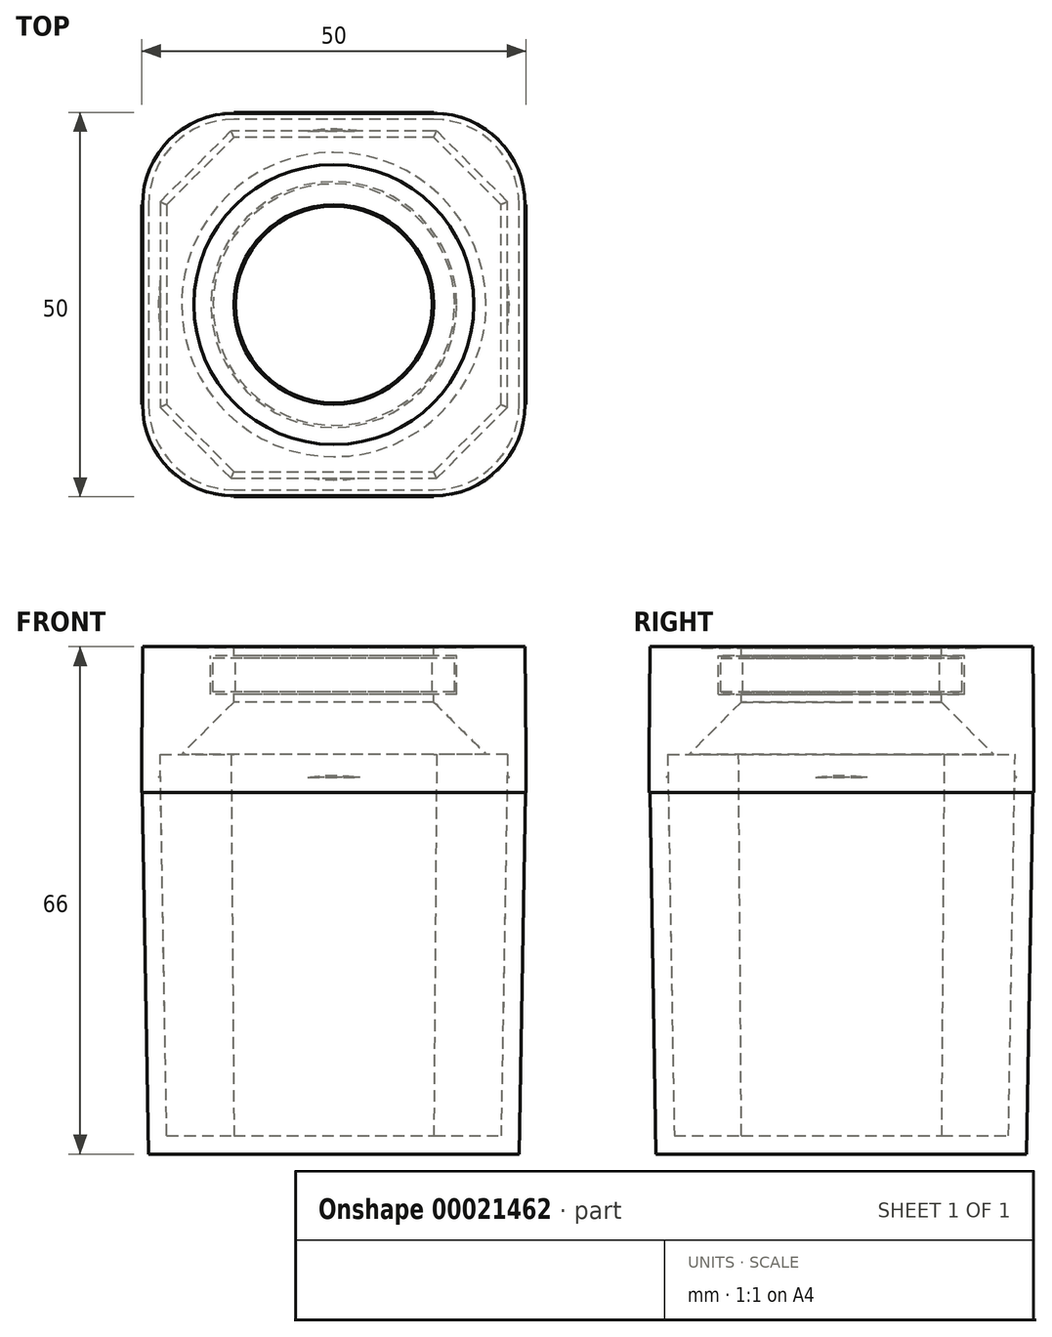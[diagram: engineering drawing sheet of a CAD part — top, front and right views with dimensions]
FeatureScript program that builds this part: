
annotation { "Feature Type Name" : "Feature", "Feature Type Description" : "" }
export const myFeature = defineFeature(function(context is Context, id is Id, definition is map)
    precondition{}
    {
        {
            var Q0;
            Q0=qCreatedBy(makeId("Top.planeOp"),FACE);
            var sketch = newSketch(context, id + "F0", { "sketchPlane" : qUnion([Q0])});
            skLineSegment(sketch, "E0.rect.bottom", {"start": v(13, 25) * mm, "end": v(-13, 25) * mm});
            skLineSegment(sketch, "E0.rect.top", {"start": v(13, -25) * mm, "end": v(-13, -25) * mm});
            skLineSegment(sketch, "E0.rect.left", {"start": v(25, 13) * mm, "end": v(25, -13) * mm});
            skLineSegment(sketch, "E0.rect.right", {"start": v(-25, 13) * mm, "end": v(-25, -13) * mm});
            skPoint(sketch, "E0.rect.middle", {"position": v(0, 0) * mm});
            skPoint(sketch, "E1.visualSharp", {"position": v(-25, 25) * mm});
            skArc(sketch, "E1.filletArc", {"start": v(-13, 25) * mm, "mid": v(-21.49, 21.49) * mm, "end": v(-25, 13) * mm});
            skPoint(sketch, "E2.visualSharp", {"position": v(25, 25) * mm});
            skArc(sketch, "E2.filletArc", {"start": v(25, 13) * mm, "mid": v(21.49, 21.49) * mm, "end": v(13, 25) * mm});
            skPoint(sketch, "E3.visualSharp", {"position": v(25, -25) * mm});
            skArc(sketch, "E3.filletArc", {"start": v(13, -25) * mm, "mid": v(21.49, -21.49) * mm, "end": v(25, -13) * mm});
            skPoint(sketch, "E4.visualSharp", {"position": v(-25, -25) * mm});
            skArc(sketch, "E4.filletArc", {"start": v(-25, -13) * mm, "mid": v(-21.49, -21.49) * mm, "end": v(-13, -25) * mm});
            skSolve(sketch);
        }
        {
            var Q0;
            Q0 = qSketchRegion(id + "F0", true);
            extrude(context, id + "F1", {"entities" : qUnion([Q0]), "oppositeDirection" : true, "depth" : 52 * mm, "hasDraft" : true, "draftAngle" : 1 * degree, "draftPullDirection" : true});
        }
        {
            var Q0;
            Q0=makeQuery(id+"F1.opExtrude","CAP_FACE",FACE,{"disambiguationData":[OSD([sQuery(id+"F0.wireOp",EDGE,"E0.rect.bottom"),sQuery(id+"F0.wireOp",EDGE,"E0.rect.top"),sQuery(id+"F0.wireOp",EDGE,"E0.rect.left"),sQuery(id+"F0.wireOp",EDGE,"E0.rect.right"),sQuery(id+"F0.wireOp",EDGE,"E1.filletArc"),sQuery(id+"F0.wireOp",EDGE,"E2.filletArc"),sQuery(id+"F0.wireOp",EDGE,"E3.filletArc"),sQuery(id+"F0.wireOp",EDGE,"E4.filletArc")])],"isStart":true});
            shell(context, id + "F2", {"entities" : qUnion([Q0]), "thickness" : 2.4 * mm});
        }
        {
            var Q0;
            Q0=makeQuery(id+"F2.opShell","OFFSET_FACE",FACE,{"disambiguationData":[OSD([sQuery(id+"F0.wireOp",EDGE,"E0.rect.bottom"),sQuery(id+"F0.wireOp",EDGE,"E0.rect.top"),sQuery(id+"F0.wireOp",EDGE,"E0.rect.left"),sQuery(id+"F0.wireOp",EDGE,"E0.rect.right"),sQuery(id+"F0.wireOp",EDGE,"E1.filletArc"),sQuery(id+"F0.wireOp",EDGE,"E2.filletArc"),sQuery(id+"F0.wireOp",EDGE,"E3.filletArc"),sQuery(id+"F0.wireOp",EDGE,"E4.filletArc")])]});
            var sketch = newSketch(context, id + "F3", { "sketchPlane" : qUnion([Q0])});
            skLineSegment(sketch, "E5", {"start": v(-13, 21.73) * mm, "end": v(-21.73, 13) * mm});
            skLineSegment(sketch, "E6", {"start": v(13, 21.73) * mm, "end": v(21.73, 13) * mm});
            skLineSegment(sketch, "E7", {"start": v(21.73, -13) * mm, "end": v(13, -21.73) * mm});
            skLineSegment(sketch, "E8", {"start": v(-13, -21.73) * mm, "end": v(-21.73, -13) * mm});
            skSolve(sketch);
        }
        {
            var Q0;
            Q0=sQuery(id+"F3.wireOp",EDGE,"E6");
            cPlane(context, id + "F4", {"entities" : qUnion([Q0]), "cplaneType" : CPlaneType.LINE_ANGLE, "offset" : 150 * mm, "angle" : 179 * degree, "width" : 150 * mm, "height" : 150 * mm});
        }
        {
            var Q0;
            Q0=sQuery(id+"F3.wireOp",EDGE,"E5");
            cPlane(context, id + "F5", {"entities" : qUnion([Q0]), "cplaneType" : CPlaneType.LINE_ANGLE, "offset" : 150 * mm, "angle" : 1 * degree, "width" : 150 * mm, "height" : 150 * mm});
        }
        {
            var Q0;
            Q0=sQuery(id+"F3.wireOp",EDGE,"E8");
            cPlane(context, id + "F6", {"entities" : qUnion([Q0]), "cplaneType" : CPlaneType.LINE_ANGLE, "offset" : 150 * mm, "angle" : 179 * degree, "width" : 150 * mm, "height" : 150 * mm});
        }
        {
            var Q0;
            Q0=sQuery(id+"F3.wireOp",EDGE,"E7");
            cPlane(context, id + "F7", {"entities" : qUnion([Q0]), "cplaneType" : CPlaneType.LINE_ANGLE, "offset" : 150 * mm, "angle" : 179 * degree, "width" : 150 * mm, "height" : 150 * mm});
        }
        {
            var Q0;
            Q0=qCreatedBy(id+"F4.planeOp",FACE);
            var sketch = newSketch(context, id + "F8", { "sketchPlane" : qUnion([Q0])});
            skLineSegment(sketch, "E9.0", {"start": v(13.6, 22.34) * mm, "end": v(22.34, 13.61) * mm});
            skLineSegment(sketch, "E10", {"start": v(13.6, 22.34) * mm, "end": v(12.9, 23.05) * mm});
            skLineSegment(sketch, "E11", {"start": v(22.34, 13.61) * mm, "end": v(23.05, 12.9) * mm});
            skArc(sketch, "E12", {"start": v(23.05, 12.9) * mm, "mid": v(20.3, 20.3) * mm, "end": v(12.9, 23.05) * mm});
            skSolve(sketch);
        }
        {
            var Q0;
            Q0=makeQuery(id+"F8.imprint","IMPRINT",FACE,{"disambiguationData":[TD([[makeQuery(id+"F8.imprint","IMPRINT",EDGE,{"derivedFrom":sQuery(id+"F8.wireOp",EDGE,"E9.0")}),1.0]])]});
            var Q1;
            Q1=makeQuery(id+"F1.opExtrude","CAP_FACE",FACE,{"disambiguationData":[OSD([sQuery(id+"F0.wireOp",EDGE,"E0.rect.bottom"),sQuery(id+"F0.wireOp",EDGE,"E0.rect.top"),sQuery(id+"F0.wireOp",EDGE,"E0.rect.left"),sQuery(id+"F0.wireOp",EDGE,"E0.rect.right"),sQuery(id+"F0.wireOp",EDGE,"E1.filletArc"),sQuery(id+"F0.wireOp",EDGE,"E2.filletArc"),sQuery(id+"F0.wireOp",EDGE,"E3.filletArc"),sQuery(id+"F0.wireOp",EDGE,"E4.filletArc")])],"isStart":true});
            extrude(context, id + "F9", {"entities" : qUnion([Q0]), "operationType" : NewBodyOperationType.ADD, "endBound" : BoundingType.UP_TO_SURFACE, "endBoundEntityFace" : qUnion([Q1]), "depth" : 25 * mm});
        }
        {
            var Q0;
            Q0=qCreatedBy(id+"F5.planeOp",FACE);
            var sketch = newSketch(context, id + "F10", { "sketchPlane" : qUnion([Q0])});
            skLineSegment(sketch, "E13.0", {"start": v(-13.6, -22.34) * mm, "end": v(-22.34, -13.61) * mm});
            skLineSegment(sketch, "E14", {"start": v(-22.34, -13.61) * mm, "end": v(-23.05, -12.9) * mm});
            skLineSegment(sketch, "E15", {"start": v(-13.6, -22.34) * mm, "end": v(-12.9, -23.05) * mm});
            skArc(sketch, "E16", {"start": v(-23.05, -12.9) * mm, "mid": v(-20.3, -20.3) * mm, "end": v(-12.9, -23.05) * mm});
            skSolve(sketch);
        }
        {
            var Q0;
            Q0=makeQuery(id+"F10.imprint","IMPRINT",FACE,{"disambiguationData":[TD([[makeQuery(id+"F10.imprint","IMPRINT",EDGE,{"derivedFrom":sQuery(id+"F10.wireOp",EDGE,"E13.0")}),1.0]])]});
            var Q1;
            {var subQ0=sQuery(id+"F0.wireOp",EDGE,"E4.filletArc");var subQ1=sQuery(id+"F0.wireOp",EDGE,"E3.filletArc");var subQ2=sQuery(id+"F0.wireOp",EDGE,"E2.filletArc");var subQ3=sQuery(id+"F0.wireOp",EDGE,"E1.filletArc");var subQ4=sQuery(id+"F0.wireOp",EDGE,"E0.rect.right");var subQ5=sQuery(id+"F0.wireOp",EDGE,"E0.rect.left");var subQ6=sQuery(id+"F0.wireOp",EDGE,"E0.rect.top");var subQ7=sQuery(id+"F0.wireOp",EDGE,"E0.rect.bottom");Q1=makeQuery(id+"F9.boolean.opBoolean","MERGE",FACE,{"derivedFrom":[makeQuery(id+"F1.opExtrude","CAP_FACE",FACE,{"disambiguationData":[OSD([subQ7,subQ6,subQ5,subQ4,subQ3,subQ2,subQ1,subQ0])],"isStart":true}),makeQuery(id+"F9.opExtrude","CAP_FACE",FACE,{"disambiguationData":[OSD([subQ7,subQ6,subQ5,subQ4,subQ3,subQ2,subQ1,subQ0])],"isStart":false})]});}
            extrude(context, id + "F11", {"entities" : qUnion([Q0]), "operationType" : NewBodyOperationType.ADD, "endBound" : BoundingType.UP_TO_SURFACE, "oppositeDirection" : true, "endBoundEntityFace" : qUnion([Q1]), "depth" : 25 * mm});
        }
        {
            var Q0;
            Q0=qCreatedBy(id+"F6.planeOp",FACE);
            var sketch = newSketch(context, id + "F12", { "sketchPlane" : qUnion([Q0])});
            skLineSegment(sketch, "E17.0", {"start": v(-13.6, 22.34) * mm, "end": v(-22.34, 13.61) * mm});
            skLineSegment(sketch, "E18", {"start": v(-22.34, 13.61) * mm, "end": v(-23.05, 12.9) * mm});
            skLineSegment(sketch, "E19", {"start": v(-13.6, 22.34) * mm, "end": v(-12.9, 23.05) * mm});
            skArc(sketch, "E20", {"start": v(-12.9, 23.05) * mm, "mid": v(-20.3, 20.3) * mm, "end": v(-23.05, 12.9) * mm});
            skSolve(sketch);
        }
        {
            var Q0;
            Q0=makeQuery(id+"F12.imprint","IMPRINT",FACE,{"disambiguationData":[TD([[makeQuery(id+"F12.imprint","IMPRINT",EDGE,{"derivedFrom":sQuery(id+"F12.wireOp",EDGE,"E17.0")}),-1.0]])]});
            var Q1;
            {var subQ0=sQuery(id+"F0.wireOp",EDGE,"E4.filletArc");var subQ1=sQuery(id+"F0.wireOp",EDGE,"E3.filletArc");var subQ2=sQuery(id+"F0.wireOp",EDGE,"E2.filletArc");var subQ3=sQuery(id+"F0.wireOp",EDGE,"E1.filletArc");var subQ4=sQuery(id+"F0.wireOp",EDGE,"E0.rect.right");var subQ5=sQuery(id+"F0.wireOp",EDGE,"E0.rect.left");var subQ6=sQuery(id+"F0.wireOp",EDGE,"E0.rect.top");var subQ7=sQuery(id+"F0.wireOp",EDGE,"E0.rect.bottom");Q1=makeQuery(id+"F11.boolean.opBoolean","MERGE",FACE,{"derivedFrom":[makeQuery(id+"F9.boolean.opBoolean","MERGE",FACE,{"derivedFrom":[makeQuery(id+"F1.opExtrude","CAP_FACE",FACE,{"disambiguationData":[OSD([subQ7,subQ6,subQ5,subQ4,subQ3,subQ2,subQ1,subQ0])],"isStart":true}),makeQuery(id+"F9.opExtrude","CAP_FACE",FACE,{"disambiguationData":[OSD([subQ7,subQ6,subQ5,subQ4,subQ3,subQ2,subQ1,subQ0])],"isStart":false})]}),makeQuery(id+"F11.opExtrude","CAP_FACE",FACE,{"disambiguationData":[OSD([subQ7,subQ6,subQ5,subQ4,subQ3,subQ2,subQ1,subQ0])],"isStart":false})]});}
            extrude(context, id + "F13", {"entities" : qUnion([Q0]), "operationType" : NewBodyOperationType.ADD, "endBound" : BoundingType.UP_TO_SURFACE, "oppositeDirection" : true, "endBoundEntityFace" : qUnion([Q1]), "depth" : 25 * mm});
        }
        {
            var Q0;
            Q0=qCreatedBy(id+"F7.planeOp",FACE);
            var sketch = newSketch(context, id + "F14", { "sketchPlane" : qUnion([Q0])});
            skLineSegment(sketch, "E21.0", {"start": v(22.34, -13.61) * mm, "end": v(13.6, -22.34) * mm});
            skLineSegment(sketch, "E22", {"start": v(13.6, -22.34) * mm, "end": v(12.9, -23.05) * mm});
            skLineSegment(sketch, "E23", {"start": v(22.34, -13.61) * mm, "end": v(23.05, -12.9) * mm});
            skArc(sketch, "E24", {"start": v(12.9, -23.05) * mm, "mid": v(20.3, -20.3) * mm, "end": v(23.05, -12.9) * mm});
            skSolve(sketch);
        }
        {
            var Q0;
            Q0=makeQuery(id+"F14.imprint","IMPRINT",FACE,{"disambiguationData":[TD([[makeQuery(id+"F14.imprint","IMPRINT",EDGE,{"derivedFrom":sQuery(id+"F14.wireOp",EDGE,"E21.0")}),1.0]])]});
            var Q1;
            {var subQ0=sQuery(id+"F0.wireOp",EDGE,"E4.filletArc");var subQ1=sQuery(id+"F0.wireOp",EDGE,"E3.filletArc");var subQ2=sQuery(id+"F0.wireOp",EDGE,"E2.filletArc");var subQ3=sQuery(id+"F0.wireOp",EDGE,"E1.filletArc");var subQ4=sQuery(id+"F0.wireOp",EDGE,"E0.rect.right");var subQ5=sQuery(id+"F0.wireOp",EDGE,"E0.rect.left");var subQ6=sQuery(id+"F0.wireOp",EDGE,"E0.rect.top");var subQ7=sQuery(id+"F0.wireOp",EDGE,"E0.rect.bottom");Q1=makeQuery(id+"F13.boolean.opBoolean","MERGE",FACE,{"derivedFrom":[makeQuery(id+"F11.boolean.opBoolean","MERGE",FACE,{"derivedFrom":[makeQuery(id+"F9.boolean.opBoolean","MERGE",FACE,{"derivedFrom":[makeQuery(id+"F1.opExtrude","CAP_FACE",FACE,{"disambiguationData":[OSD([subQ7,subQ6,subQ5,subQ4,subQ3,subQ2,subQ1,subQ0])],"isStart":true}),makeQuery(id+"F9.opExtrude","CAP_FACE",FACE,{"disambiguationData":[OSD([subQ7,subQ6,subQ5,subQ4,subQ3,subQ2,subQ1,subQ0])],"isStart":false})]}),makeQuery(id+"F11.opExtrude","CAP_FACE",FACE,{"disambiguationData":[OSD([subQ7,subQ6,subQ5,subQ4,subQ3,subQ2,subQ1,subQ0])],"isStart":false})]}),makeQuery(id+"F13.opExtrude","CAP_FACE",FACE,{"disambiguationData":[OSD([subQ7,subQ6,subQ5,subQ4,subQ3,subQ2,subQ1,subQ0])],"isStart":false})]});}
            extrude(context, id + "F15", {"entities" : qUnion([Q0]), "operationType" : NewBodyOperationType.ADD, "endBound" : BoundingType.UP_TO_SURFACE, "endBoundEntityFace" : qUnion([Q1]), "depth" : 25 * mm});
        }
        {
            var Q0;
            Q0=qCreatedBy(makeId("Top.planeOp"),FACE);
            var sketch = newSketch(context, id + "F16", { "sketchPlane" : qUnion([Q0])});
            skLineSegment(sketch, "E25.0", {"start": v(-25, 13) * mm, "end": v(-25, -13) * mm});
            skArc(sketch, "E25.1", {"start": v(-13, 25) * mm, "mid": v(-21.49, 21.49) * mm, "end": v(-25, 13) * mm});
            skLineSegment(sketch, "E25.2", {"start": v(13, 25) * mm, "end": v(-13, 25) * mm});
            skArc(sketch, "E25.3", {"start": v(25, 13) * mm, "mid": v(21.49, 21.49) * mm, "end": v(13, 25) * mm});
            skLineSegment(sketch, "E25.4", {"start": v(25, 13) * mm, "end": v(25, -13) * mm});
            skArc(sketch, "E25.5", {"start": v(13, -25) * mm, "mid": v(21.49, -21.49) * mm, "end": v(25, -13) * mm});
            skLineSegment(sketch, "E25.6", {"start": v(13, -25) * mm, "end": v(-13, -25) * mm});
            skArc(sketch, "E25.7", {"start": v(-25, -13) * mm, "mid": v(-21.49, -21.49) * mm, "end": v(-13, -25) * mm});
            skLineSegment(sketch, "E26.0", {"start": v(13, 23.8) * mm, "end": v(-13, 23.8) * mm});
            skArc(sketch, "E26.1", {"start": v(23.8, 13) * mm, "mid": v(20.64, 20.64) * mm, "end": v(13, 23.8) * mm});
            skLineSegment(sketch, "E26.2", {"start": v(23.8, 13) * mm, "end": v(23.8, -13) * mm});
            skArc(sketch, "E26.3", {"start": v(13, -23.8) * mm, "mid": v(20.64, -20.64) * mm, "end": v(23.8, -13) * mm});
            skLineSegment(sketch, "E26.4", {"start": v(13, -23.8) * mm, "end": v(-13, -23.8) * mm});
            skArc(sketch, "E26.5", {"start": v(-13, 23.8) * mm, "mid": v(-20.64, 20.64) * mm, "end": v(-23.8, 13) * mm});
            skArc(sketch, "E26.6", {"start": v(-23.8, -13) * mm, "mid": v(-20.64, -20.64) * mm, "end": v(-13, -23.8) * mm});
            skLineSegment(sketch, "E26.7", {"start": v(-23.8, 13) * mm, "end": v(-23.8, -13) * mm});
            skSolve(sketch);
        }
        {
            var Q0;
            Q0=makeQuery(id+"F16.imprint","IMPRINT",FACE,{"disambiguationData":[TD([[makeQuery(id+"F16.imprint","IMPRINT",EDGE,{"derivedFrom":sQuery(id+"F16.wireOp",EDGE,"E25.0")}),1.0]])]});
            extrude(context, id + "F17", {"entities" : qUnion([Q0]), "depth" : 14 * mm, "hasDraft" : true, "draftAngle" : .5 * degree, "draftPullDirection" : true, "hasSecondDirection" : true, "secondDirectionOppositeDirection" : true, "secondDirectionDepth" : 5 * mm});
        }
        {
            var Q0;
            Q0=makeQuery(id+"F17.split0.splitOp","SPLIT",BODY,{"derivedFrom":makeQuery(id+"F17.opExtrude","SWEPT_BODY",BODY,{"disambiguationData":[OSD([sQuery(id+"F16.wireOp",EDGE,"E25.0"),sQuery(id+"F16.wireOp",EDGE,"E25.1"),sQuery(id+"F16.wireOp",EDGE,"E25.2"),sQuery(id+"F16.wireOp",EDGE,"E25.3"),sQuery(id+"F16.wireOp",EDGE,"E25.4"),sQuery(id+"F16.wireOp",EDGE,"E25.5"),sQuery(id+"F16.wireOp",EDGE,"E25.6"),sQuery(id+"F16.wireOp",EDGE,"E25.7"),sQuery(id+"F16.wireOp",EDGE,"E26.0"),sQuery(id+"F16.wireOp",EDGE,"E26.1"),sQuery(id+"F16.wireOp",EDGE,"E26.2"),sQuery(id+"F16.wireOp",EDGE,"E26.3"),sQuery(id+"F16.wireOp",EDGE,"E26.4"),sQuery(id+"F16.wireOp",EDGE,"E26.5"),sQuery(id+"F16.wireOp",EDGE,"E26.6"),sQuery(id+"F16.wireOp",EDGE,"E26.7")])]})});
            var Q1;
            Q1=makeQuery(id+"F1.opExtrude","SWEPT_BODY",BODY,{"disambiguationData":[OSD([sQuery(id+"F0.wireOp",EDGE,"E0.rect.bottom"),sQuery(id+"F0.wireOp",EDGE,"E0.rect.top"),sQuery(id+"F0.wireOp",EDGE,"E0.rect.left"),sQuery(id+"F0.wireOp",EDGE,"E0.rect.right"),sQuery(id+"F0.wireOp",EDGE,"E1.filletArc"),sQuery(id+"F0.wireOp",EDGE,"E2.filletArc"),sQuery(id+"F0.wireOp",EDGE,"E3.filletArc"),sQuery(id+"F0.wireOp",EDGE,"E4.filletArc")])]});
            booleanBodies(context, id + "F18", {"operationType" : BooleanOperationType.SUBTRACTION, "tools" : qUnion([Q0]), "targets" : qUnion([Q1]), "keepTools" : true});
        }
        {
            var Q0;
            Q0=qCreatedBy(makeId("Top.planeOp"),FACE);
            var sketch = newSketch(context, id + "F19", { "sketchPlane" : qUnion([Q0])});
            skArc(sketch, "E27.0", {"start": v(13, -23.8) * mm, "mid": v(20.64, -20.64) * mm, "end": v(23.8, -13) * mm});
            skLineSegment(sketch, "E27.1", {"start": v(13, -23.8) * mm, "end": v(-13, -23.8) * mm});
            skArc(sketch, "E27.2", {"start": v(-23.8, -13) * mm, "mid": v(-20.64, -20.64) * mm, "end": v(-13, -23.8) * mm});
            skLineSegment(sketch, "E27.3", {"start": v(23.8, 13) * mm, "end": v(23.8, -13) * mm});
            skArc(sketch, "E27.4", {"start": v(23.8, 13) * mm, "mid": v(20.64, 20.64) * mm, "end": v(13, 23.8) * mm});
            skLineSegment(sketch, "E27.5", {"start": v(13, 23.8) * mm, "end": v(-13, 23.8) * mm});
            skArc(sketch, "E27.6", {"start": v(-13, 23.8) * mm, "mid": v(-20.64, 20.64) * mm, "end": v(-23.8, 13) * mm});
            skLineSegment(sketch, "E27.7", {"start": v(-23.8, 13) * mm, "end": v(-23.8, -13) * mm});
            skSolve(sketch);
        }
        {
            var Q0;
            Q0=makeQuery(id+"F19.imprint","IMPRINT",FACE,{"disambiguationData":[TD([[makeQuery(id+"F19.imprint","IMPRINT",EDGE,{"derivedFrom":sQuery(id+"F19.wireOp",EDGE,"E27.0")}),1.0]])]});
            var Q1;
            Q1=makeQuery(id+"F17.opExtrude","CAP_FACE",FACE,{"disambiguationData":[OSD([sQuery(id+"F16.wireOp",EDGE,"E25.0"),sQuery(id+"F16.wireOp",EDGE,"E25.1"),sQuery(id+"F16.wireOp",EDGE,"E25.2"),sQuery(id+"F16.wireOp",EDGE,"E25.3"),sQuery(id+"F16.wireOp",EDGE,"E25.4"),sQuery(id+"F16.wireOp",EDGE,"E25.5"),sQuery(id+"F16.wireOp",EDGE,"E25.6"),sQuery(id+"F16.wireOp",EDGE,"E25.7"),sQuery(id+"F16.wireOp",EDGE,"E26.0"),sQuery(id+"F16.wireOp",EDGE,"E26.1"),sQuery(id+"F16.wireOp",EDGE,"E26.2"),sQuery(id+"F16.wireOp",EDGE,"E26.3"),sQuery(id+"F16.wireOp",EDGE,"E26.4"),sQuery(id+"F16.wireOp",EDGE,"E26.5"),sQuery(id+"F16.wireOp",EDGE,"E26.6"),sQuery(id+"F16.wireOp",EDGE,"E26.7")])],"isStart":false});
            extrude(context, id + "F20", {"entities" : qUnion([Q0]), "operationType" : NewBodyOperationType.ADD, "endBound" : BoundingType.UP_TO_SURFACE, "endBoundEntityFace" : qUnion([Q1]), "depth" : 25 * mm, "hasDraft" : true, "draftAngle" : 1 * degree});
        }
        {
            var Q0;
            Q0=qCreatedBy(makeId("Right.planeOp"),FACE);
            var sketch = newSketch(context, id + "F21", { "sketchPlane" : qUnion([Q0])});
            skLineSegment(sketch, "E28.0", {"start": v(13, 14) * mm, "end": v(-13, 14) * mm});
            skLineSegment(sketch, "E29", {"start": v(18.2, 13.8) * mm, "end": v(13, 13.8) * mm});
            skLineSegment(sketch, "E30", {"start": v(13, 13.8) * mm, "end": v(13, 12.8) * mm});
            skLineSegment(sketch, "E31", {"start": v(13, 12.8) * mm, "end": v(16, 12.8) * mm});
            skLineSegment(sketch, "E32", {"start": v(16, 12.8) * mm, "end": v(16, 7.8) * mm});
            skLineSegment(sketch, "E33", {"start": v(16, 7.8) * mm, "end": v(13, 7.8) * mm});
            skLineSegment(sketch, "E34", {"start": v(13, 7.8) * mm, "end": v(13, 6.8) * mm});
            skLineSegment(sketch, "E35", {"start": v(13, 6.8) * mm, "end": v(22.8, -3) * mm});
            skLineSegment(sketch, "E36", {"start": v(22.8, -3) * mm, "end": v(0, -3) * mm});
            skLineSegment(sketch, "E37", {"start": v(0, -3) * mm, "end": v(0, 17) * mm});
            skLineSegment(sketch, "E38", {"start": v(0, 17) * mm, "end": v(18.2, 17) * mm});
            skLineSegment(sketch, "E39", {"start": v(18.2, 17) * mm, "end": v(18.2, 13.8) * mm});
            skLineSegment(sketch, "E40.0", {"start": v(13, 0) * mm, "end": v(-13, 0) * mm});
            skLineSegment(sketch, "E41.bottom", {"start": v(15.7, 8.1) * mm, "end": v(12.8, 8.1) * mm});
            skLineSegment(sketch, "E41.top", {"start": v(15.7, 12.5) * mm, "end": v(12.8, 12.5) * mm});
            skLineSegment(sketch, "E41.left", {"start": v(15.7, 8.1) * mm, "end": v(15.7, 12.5) * mm});
            skLineSegment(sketch, "E41.right", {"start": v(12.8, 8.1) * mm, "end": v(12.8, 12.5) * mm});
            skSolve(sketch);
        }
        {
            var Q0;
            Q0=makeQuery(id+"F21.imprint","IMPRINT",FACE,{"disambiguationData":[TD([[makeQuery(id+"F21.imprint","IMPRINT",EDGE,{"derivedFrom":sQuery(id+"F21.wireOp",EDGE,"E29")}),-1.0]])]});
            var Q1;
            Q1=sQuery(id+"F21.wireOp",EDGE,"E37");
            revolve(context, id + "F22", {"operationType" : NewBodyOperationType.REMOVE, "entities" : qUnion([Q0]), "axis" : qUnion([Q1]), "revolveType" : RevolveType.FULL, "oppositeDirection" : true});
        }
    });
